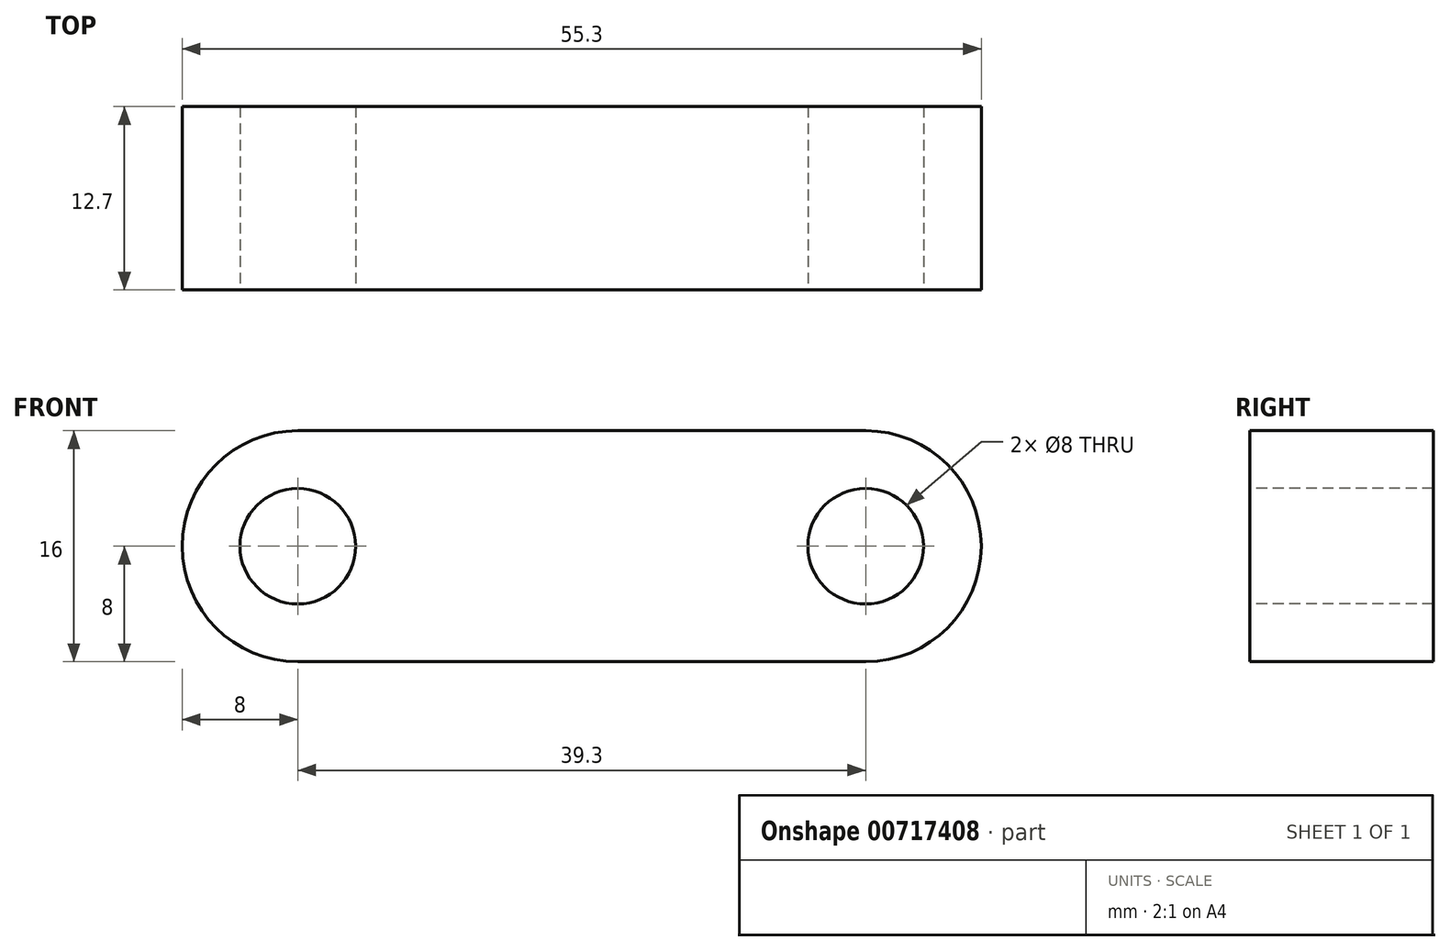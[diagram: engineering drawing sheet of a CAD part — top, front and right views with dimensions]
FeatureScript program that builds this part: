
annotation { "Feature Type Name" : "Feature", "Feature Type Description" : "" }
export const myFeature = defineFeature(function(context is Context, id is Id, definition is map)
    precondition{}
    {
        {
            var Q0;
            Q0=qCreatedBy(makeId("Front.planeOp"),FACE);
            var sketch = newSketch(context, id + "F0", { "sketchPlane" : qUnion([Q0])});
            skCircle(sketch, "E0", {"center": v(-39.3, 0) * mm, "radius": 8 * mm});
            skCircle(sketch, "E1", {"center": v(0, 0) * mm, "radius": 8 * mm});
            skLineSegment(sketch, "E2", {"start": v(-39.3, 8) * mm, "end": v(0, 8) * mm});
            skLineSegment(sketch, "E3", {"start": v(0, -8) * mm, "end": v(-39.3, -8) * mm});
            skSolve(sketch);
        }
        {
            var Q0;
            {var subQ0=sQuery(id+"F0.wireOp",EDGE,"E2");Q0=makeQuery(id+"F0.imprint","IMPRINT",FACE,{"disambiguationData":[TD([[makeQuery(id+"F0.imprint","IMPRINT",EDGE,{"derivedFrom":subQ0}),-1.0]])]});}
            var Q1;
            {var subQ0=sQuery(id+"F0.wireOp",EDGE,"E0");var subQ1=makeQuery(id+"F0.imprint","INTERSECT",VERTEX,{"derivedFrom":[subQ0,sQuery(id+"F0.wireOp",EDGE,"E2")]});Q1=makeQuery(id+"F0.imprint","IMPRINT",FACE,{"disambiguationData":[TD([[makeQuery(id+"F0.imprint","IMPRINT",EDGE,{"disambiguationData":[TD([[subQ1,-1.0]])],"derivedFrom":subQ0}),1.0]])]});}
            var Q2;
            {var subQ0=sQuery(id+"F0.wireOp",EDGE,"E1");var subQ1=makeQuery(id+"F0.imprint","INTERSECT",VERTEX,{"derivedFrom":[subQ0,sQuery(id+"F0.wireOp",EDGE,"E2")]});Q2=makeQuery(id+"F0.imprint","IMPRINT",FACE,{"disambiguationData":[TD([[makeQuery(id+"F0.imprint","IMPRINT",EDGE,{"disambiguationData":[TD([[subQ1,-1.0]])],"derivedFrom":subQ0}),1.0]])]});}
            extrude(context, id + "F1", {"entities" : qUnion([Q0, Q1, Q2]), "depth" : 12.7 * mm, "offsetDistance" : 25.4 * mm});
        }
        {
            var Q0;
            Q0=makeQuery(id+"F1.opExtrude","CAP_FACE",FACE,{"disambiguationData":[OSD([sQuery(id+"F0.wireOp",EDGE,"E0"),sQuery(id+"F0.wireOp",EDGE,"E1"),sQuery(id+"F0.wireOp",EDGE,"E2"),sQuery(id+"F0.wireOp",EDGE,"E3")])],"isStart":false});
            var sketch = newSketch(context, id + "F2", { "sketchPlane" : qUnion([Q0])});
            skCircle(sketch, "E4", {"center": v(-39.3, 0) * mm, "radius": 4 * mm});
            skCircle(sketch, "E5", {"center": v(0, 0) * mm, "radius": 4 * mm});
            skSolve(sketch);
        }
        {
            var Q0;
            Q0=makeQuery(id+"F2.imprint","IMPRINT",FACE,{"disambiguationData":[TD([[makeQuery(id+"F2.imprint","IMPRINT",EDGE,{"derivedFrom":sQuery(id+"F2.wireOp",EDGE,"E4")}),1.0]])]});
            var Q1;
            Q1=makeQuery(id+"F2.imprint","IMPRINT",FACE,{"disambiguationData":[TD([[makeQuery(id+"F2.imprint","IMPRINT",EDGE,{"derivedFrom":sQuery(id+"F2.wireOp",EDGE,"E5")}),1.0]])]});
            extrude(context, id + "F3", {"entities" : qUnion([Q0, Q1]), "operationType" : NewBodyOperationType.REMOVE, "oppositeDirection" : true, "depth" : 12.7 * mm, "offsetDistance" : 25.4 * mm});
        }
    });
